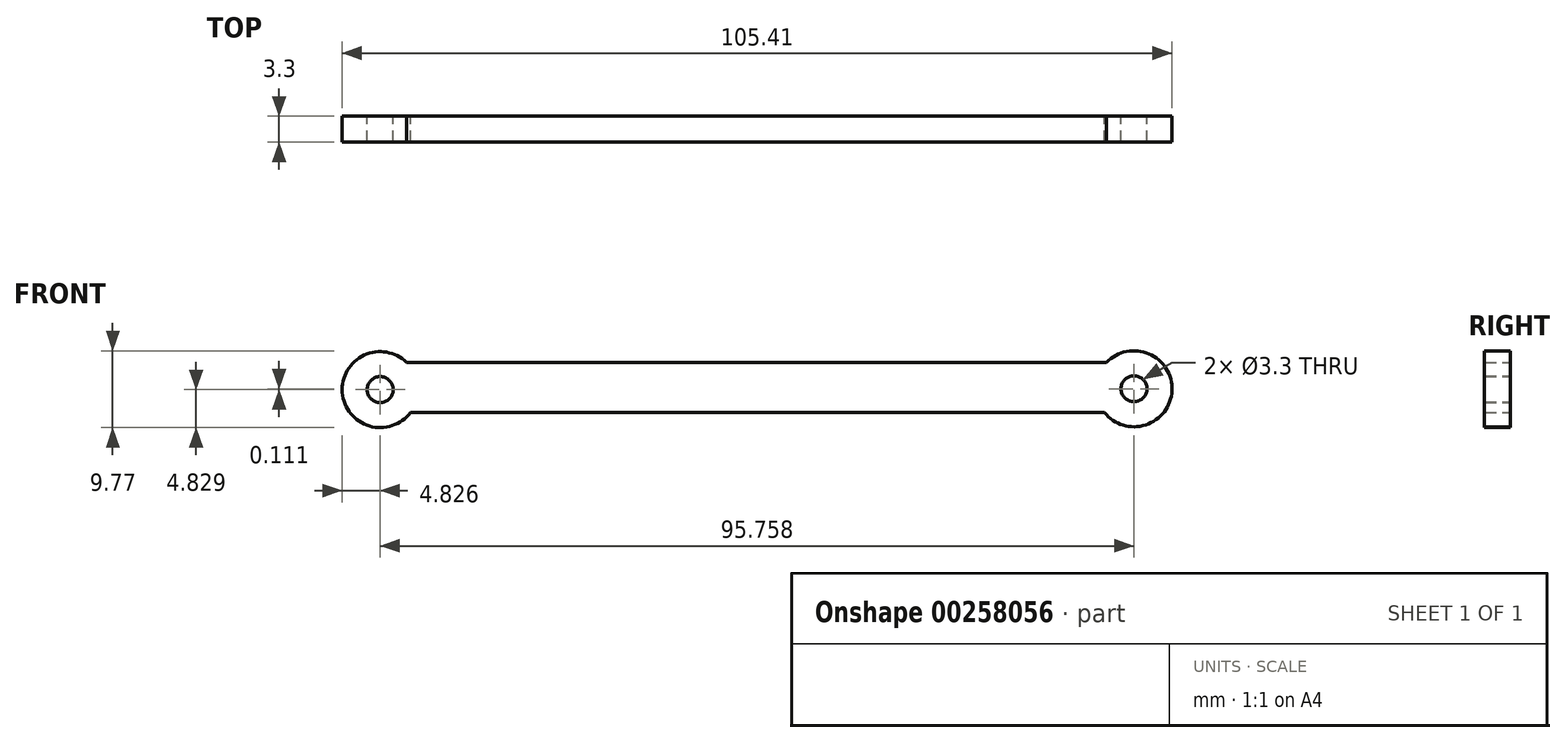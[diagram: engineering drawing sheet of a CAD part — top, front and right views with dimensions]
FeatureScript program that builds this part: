
annotation { "Feature Type Name" : "Feature", "Feature Type Description" : "" }
export const myFeature = defineFeature(function(context is Context, id is Id, definition is map)
    precondition{}
    {
        {
            var Q0;
            Q0=qCreatedBy(makeId("Front.planeOp"),FACE);
            var sketch = newSketch(context, id + "F0", { "sketchPlane" : qUnion([Q0])});
            skLineSegment(sketch, "E0", {"start": v(-35.97, 6.35) * mm, "end": v(52.93, 6.35) * mm});
            skLineSegment(sketch, "E1", {"start": v(-35.49, 0) * mm, "end": v(52.64, 0) * mm});
            skCircle(sketch, "E2", {"center": v(56.41, 3.01) * mm, "radius": 4.83 * mm});
            skCircle(sketch, "E3", {"center": v(-39.34, 2.9) * mm, "radius": 4.83 * mm});
            skCircle(sketch, "E4", {"center": v(-39.34, 2.9) * mm, "radius": 1.65 * mm});
            skCircle(sketch, "E5", {"center": v(56.41, 3.01) * mm, "radius": 1.65 * mm});
            skSolve(sketch);
        }
        {
            var Q0;
            Q0 = qSketchRegion(id + "F0", true);
            extrude(context, id + "F1", {"entities" : qUnion([Q0]), "depth" : 3.3 * mm});
        }
    });
